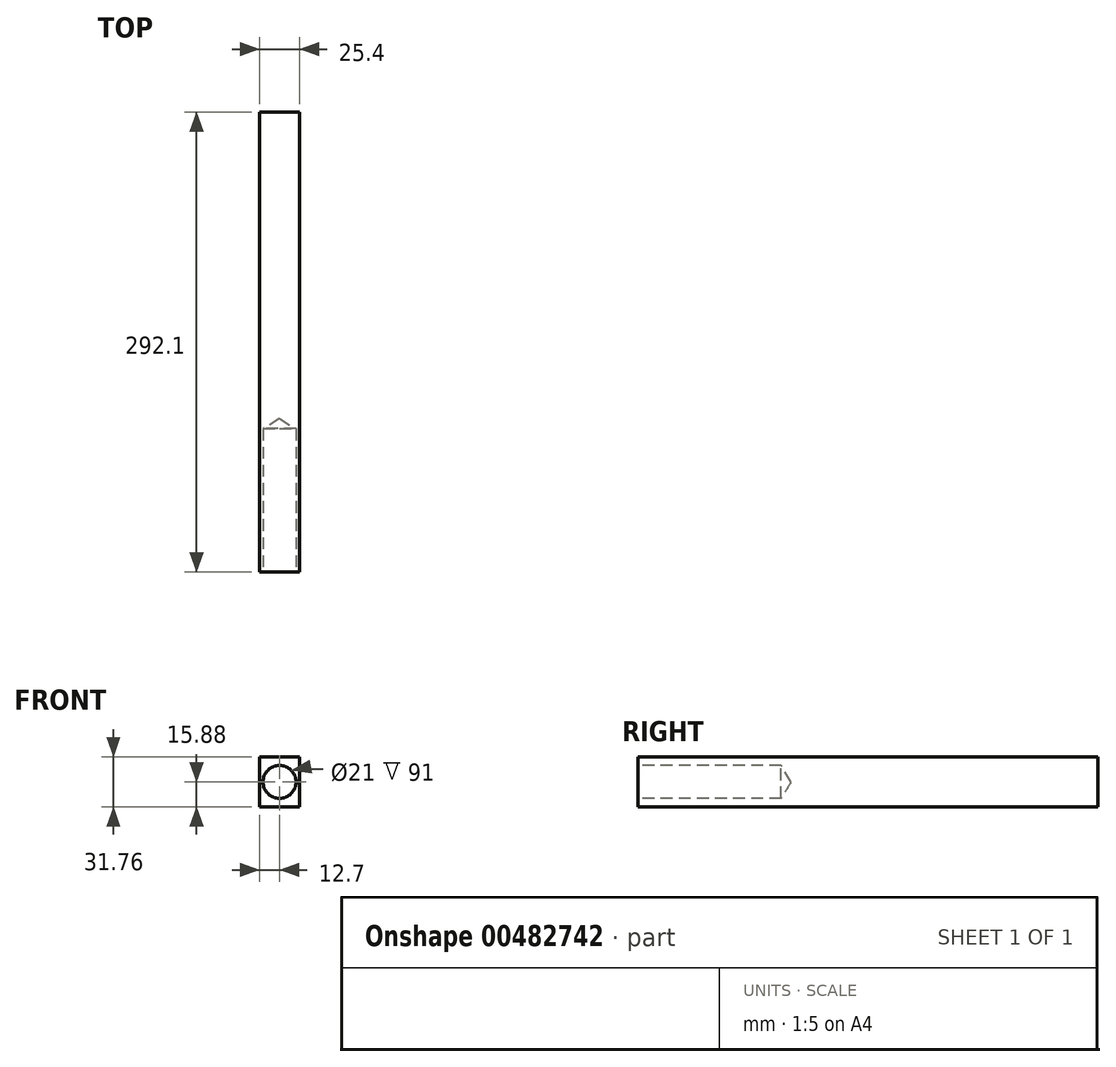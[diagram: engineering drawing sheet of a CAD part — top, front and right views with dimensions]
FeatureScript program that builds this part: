
annotation { "Feature Type Name" : "Feature", "Feature Type Description" : "" }
export const myFeature = defineFeature(function(context is Context, id is Id, definition is map)
    precondition{}
    {
        {
            var Q0;
            Q0=qCreatedBy(makeId("Right.planeOp"),FACE);
            var sketch = newSketch(context, id + "F0", { "sketchPlane" : qUnion([Q0])});
            skLineSegment(sketch, "E0.bottom", {"start": v(146.05, 15.88) * mm, "end": v(-146.05, 15.88) * mm});
            skLineSegment(sketch, "E0.top", {"start": v(146.05, -15.88) * mm, "end": v(-146.05, -15.88) * mm});
            skLineSegment(sketch, "E0.left", {"start": v(146.05, 15.88) * mm, "end": v(146.05, -15.88) * mm});
            skLineSegment(sketch, "E0.right", {"start": v(-146.05, 15.88) * mm, "end": v(-146.05, -15.88) * mm});
            skPoint(sketch, "E0.middle", {"position": v(0, 0) * mm});
            skSolve(sketch);
        }
        {
            var Q0;
            Q0=makeQuery(id+"F0.imprint","IMPRINT",FACE,{"disambiguationData":[TD([[makeQuery(id+"F0.imprint","IMPRINT",EDGE,{"derivedFrom":sQuery(id+"F0.wireOp",EDGE,"E0.bottom")}),1.0]])]});
            extrude(context, id + "F1", {"entities" : qUnion([Q0]), "depth" : 20.32 * mm});
        }
        {
            var Q0;
            Q0=makeQuery(id+"F1.opExtrude","CAP_FACE",FACE,{"disambiguationData":[OSD([sQuery(id+"F0.wireOp",EDGE,"E0.bottom"),sQuery(id+"F0.wireOp",EDGE,"E0.top"),sQuery(id+"F0.wireOp",EDGE,"E0.left"),sQuery(id+"F0.wireOp",EDGE,"E0.right")])],"isStart":false});
            extrude(context, id + "F2", {"entities" : qUnion([Q0]), "operationType" : NewBodyOperationType.ADD, "depth" : 5.08 * mm});
        }
        {
            var Q0;
            Q0=makeQuery(id+"F2.opExtrude","CAP_FACE",FACE,{"disambiguationData":[OSD([sQuery(id+"F0.wireOp",EDGE,"E0.bottom"),sQuery(id+"F0.wireOp",EDGE,"E0.top"),sQuery(id+"F0.wireOp",EDGE,"E0.left"),sQuery(id+"F0.wireOp",EDGE,"E0.right")])],"isStart":false});
            extrude(context, id + "F3", {"entities" : qUnion([Q0]), "operationType" : NewBodyOperationType.ADD, "depth" : 25.4 * mm});
        }
        {
            var Q0;
            Q0=makeQuery(id+"F3.opExtrude","CAP_FACE",FACE,{"disambiguationData":[OSD([sQuery(id+"F0.wireOp",EDGE,"E0.bottom"),sQuery(id+"F0.wireOp",EDGE,"E0.top"),sQuery(id+"F0.wireOp",EDGE,"E0.left"),sQuery(id+"F0.wireOp",EDGE,"E0.right")])],"isStart":false});
            extrude(context, id + "F4", {"entities" : qUnion([Q0]), "operationType" : NewBodyOperationType.REMOVE, "oppositeDirection" : true, "depth" : 25.4 * mm});
        }
        {
            var Q0;
            {var subQ0=sQuery(id+"F0.wireOp",EDGE,"E0.right");Q0=makeQuery(id+"F3.boolean.opBoolean","MERGE",FACE,{"derivedFrom":[makeQuery(id+"F2.boolean.opBoolean","MERGE",FACE,{"derivedFrom":[makeQuery(id+"F1.opExtrude","SWEPT_FACE",FACE,{"disambiguationData":[OSD([subQ0])]}),makeQuery(id+"F2.opExtrude","SWEPT_FACE",FACE,{"disambiguationData":[OSD([subQ0])]})]}),makeQuery(id+"F3.opExtrude","SWEPT_FACE",FACE,{"disambiguationData":[OSD([subQ0])]})]});}
            var sketch = newSketch(context, id + "F5", { "sketchPlane" : qUnion([Q0])});
            skPoint(sketch, "E1", {"position": v(12.7, 0) * mm});
            skPoint(sketch, "E1.positionSnap0", {"position": v(12.7, -15.87) * mm});
            skSolve(sketch);
        }
        {
            var Q0;
            Q0=sQuery(id+"F5.wireOp",VERTEX,"E1");
            var Q1;
            Q1=makeQuery(id+"F1.opExtrude","SWEPT_BODY",BODY,{"disambiguationData":[OSD([sQuery(id+"F0.wireOp",EDGE,"E0.bottom"),sQuery(id+"F0.wireOp",EDGE,"E0.top"),sQuery(id+"F0.wireOp",EDGE,"E0.left"),sQuery(id+"F0.wireOp",EDGE,"E0.right")])]});
            hole(context, id + "F6", {"style" : HoleStyle.SIMPLE, "endStyle" : HoleEndStyle.BLIND, "holeDiameter" : 21 * mm, "holeDepth" : 91 * mm, "isTappedThrough" : true, "tappedDepth" : 12.7 * mm, "tapClearance" : 3, "locations" : qUnion([Q0]), "scope" : qUnion([Q1])});
        }
    });
